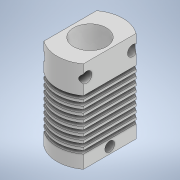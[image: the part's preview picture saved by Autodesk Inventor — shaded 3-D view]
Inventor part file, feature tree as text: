
AUTODESK INVENTOR PART (.ipt)
format: ipt  version: 2022 (Build 260153070, 153G)  size: 250,880 bytes
history: native  units: mm
features: extrude x8, sketch x6, plane x1, pattern_linear x1
ambient origin geometry x8: Origin, YZ Plane, XZ Plane, XY Plane, X Axis, Y Axis, Z Axis, Center Point
bodies: Solid1 (feature_tree)
feature tree (16):
  sketch  "Sketch1"  dims[d0=10.0mm d1=10.0mm]
  extrude  "Extrusion1"  Depth=10.0mm
  plane  "Work Plane1"
  extrude  "Extrusion2"  Depth=3.0mm
  pattern_linear  "Rectangular Pattern1"  Spacing1=-4.0mm  [1 undecoded]
  extrude  "Extrusion3"  Depth=10.0mm TaperAngle=0.0deg
  extrude  "Extrusion4"  Depth=10.0mm
  extrude  "Extrusion5"  Depth=10.0mm
  extrude  "Extrusion6"  Depth=10.0mm TaperAngle=0.0deg
  extrude  "Extrusion7"  Depth=10.0mm
  extrude  "Extrusion8"  Depth=10.0mm TaperAngle=0.0deg
  sketch  "Sketch2"  dims[d3=12.0mm d4=3.0mm]
  sketch  "Sketch3"  dims[d5=7.0mm]
  sketch  "Sketch4"  dims[d6=1.5mm]
  sketch  "Sketch5"  dims[d7=7.0mm]
  sketch  "Sketch6"  dims[d8=27.8mm d9=0.0mm d10=-4.0mm d11=1.0mm d12=0.0mm d13=90.0mm d15=1.8mm d16=8.6mm d17=16.7mm d18=0.0mm d19=6.0mm d20=3.1mm d21=0.0mm d22=10.0mm d23=8.0mm d24=0.0mm d25=4.0mm d26=0.0mm d27=3.2mm d28=23.8mm d29=14.0mm d31=7.0mm d32=12.0mm d33=0.0mm d34=2.0mm d35=3.0mm d36=4.75mm d37=0.0mm]
note: 1 required parameter value undecoded (feature->parameter linkage not recoverable at this tier; creation-order binding heuristic only, values carry confidence <= 0.55)
